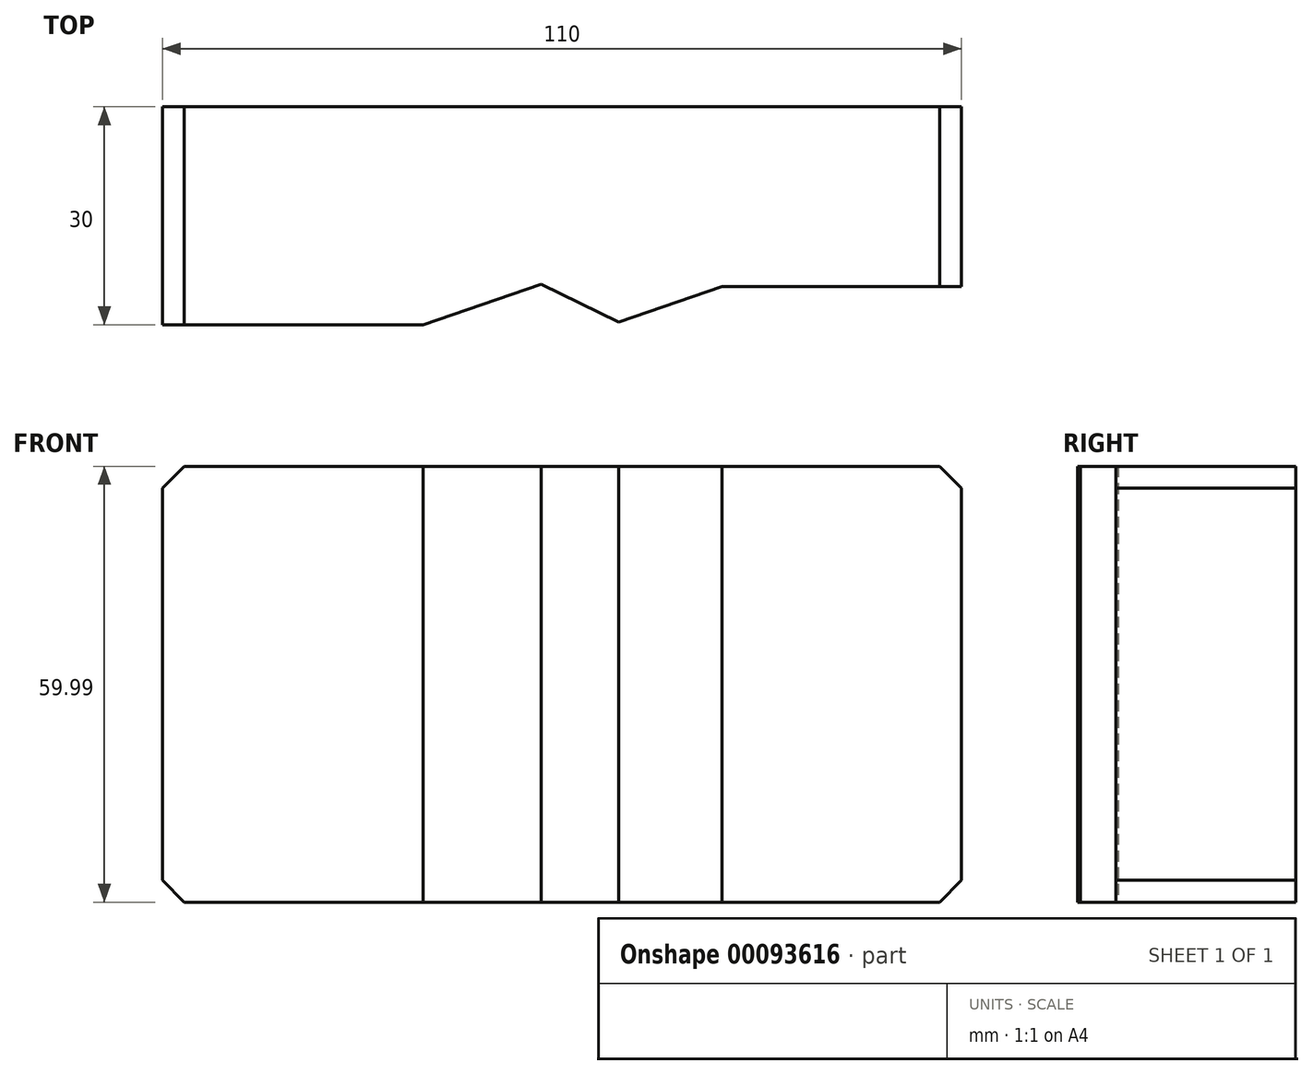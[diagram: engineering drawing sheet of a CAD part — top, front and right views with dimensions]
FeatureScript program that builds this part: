
annotation { "Feature Type Name" : "Feature", "Feature Type Description" : "" }
export const myFeature = defineFeature(function(context is Context, id is Id, definition is map)
    precondition{}
    {
        {
            var Q0;
            Q0=qCreatedBy(makeId("Top.planeOp"),FACE);
            var sketch = newSketch(context, id + "F0", { "sketchPlane" : qUnion([Q0])});
            skLineSegment(sketch, "E0", {"start": v(-59.27, 19.96) * mm, "end": v(50.73, 19.96) * mm});
            skLineSegment(sketch, "E1", {"start": v(-59.27, 19.96) * mm, "end": v(-59.27, -10.04) * mm});
            skLineSegment(sketch, "E2", {"start": v(50.73, 19.96) * mm, "end": v(50.73, -4.76) * mm});
            skLineSegment(sketch, "E3", {"start": v(-59.27, -10.04) * mm, "end": v(-23.4, -10.04) * mm});
            skPoint(sketch, "E4.orphan", {"position": v(0, -10.04) * mm});
            skLineSegment(sketch, "E5", {"start": v(-23.4, -10.04) * mm, "end": v(-7.1, -4.44) * mm});
            skLineSegment(sketch, "E6", {"start": v(-7.1, -4.44) * mm, "end": v(3.57, -9.65) * mm});
            skLineSegment(sketch, "E7", {"start": v(3.57, -9.65) * mm, "end": v(17.75, -4.76) * mm});
            skPoint(sketch, "E8.orphan", {"position": v(0, -4.76) * mm});
            skLineSegment(sketch, "E9", {"start": v(17.75, -4.76) * mm, "end": v(50.73, -4.76) * mm});
            skSolve(sketch);
        }
        {
            var Q0;
            Q0 = qSketchRegion(id + "F0", true);
            var Q1;
            Q1=makeQuery(id+"F0.imprint","IMPRINT",FACE,{"disambiguationData":[TD([[makeQuery(id+"F0.imprint","IMPRINT",EDGE,{"derivedFrom":sQuery(id+"F0.wireOp",EDGE,"E0")}),-1.0]])]});
            extrude(context, id + "F1", {"entities" : qUnion([Q0, Q1]), "depth" : 60 * mm});
        }
        {
            var Q0;
            Q0=makeQuery(id+"F1.opExtrude","CAP_EDGE",EDGE,{"disambiguationData":[OSD([sQuery(id+"F0.wireOp",EDGE,"E1")])],"isStart":true});
            var Q1;
            Q1=makeQuery(id+"F1.opExtrude","CAP_EDGE",EDGE,{"disambiguationData":[OSD([sQuery(id+"F0.wireOp",EDGE,"E2")])],"isStart":true});
            var Q2;
            Q2=makeQuery(id+"F1.opExtrude","CAP_EDGE",EDGE,{"disambiguationData":[OSD([sQuery(id+"F0.wireOp",EDGE,"E2")])],"isStart":false});
            var Q3;
            Q3=makeQuery(id+"F1.opExtrude","CAP_EDGE",EDGE,{"disambiguationData":[OSD([sQuery(id+"F0.wireOp",EDGE,"E1")])],"isStart":false});
            chamfer(context, id + "F2", {"entities" : qUnion([Q0, Q1, Q2, Q3]), "width" : 3 * mm, "tangentPropagation" : true});
        }
    });
